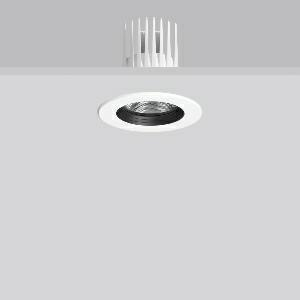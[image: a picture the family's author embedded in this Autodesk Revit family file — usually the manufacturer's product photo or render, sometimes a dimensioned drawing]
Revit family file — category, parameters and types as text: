
# Revit family: heledon_mini_e_901750_002_2_9171
name_source: partatom
category: Lighting Fixtures
units: mm (PartAtom-declared; Revit-internal decimal feet)

## family parameters
Cut with Voids When Loaded = No
Host = Face
Light Source = No
Part Type = Normal
Room Calculation Point = No
Round Connector Dimension = Use Diameter
Shared = No

## types (1)
- HELEDON mini E (1 x LED Modul 927, 3500 lm, 2700)
    Apparent Load = 29 VA
    Approval mark = CE
    CIE Flux Codes = 95 99 100 100 100
    Color Rendering = 92
    Color Temperature = 2700
    Default Elevation = 1800 mm
    Description = Series: HELEDON mini
Round recessed downlight. Housing: die-cast aluminium, powder-coated. Black plastic ring and recessed LED to prevent glare from the side. Optical assembly with reflector made of MIRO-Silver with 98% total light reflection for outstanding efficiency - can be changed without tools. Best colour rendering index Ra>90. Suitable for Recessed ceiling mounting. Installation without tools thanks to spring fastening system. Including separate LED converter with connecting cable 600 mm.High quality converter without flickering and stroboscopic effect. Through-wiring box (5 pole) available as accessory. The following accessories can be mounted without use of tools: interchangeable lenses, decorative glasses, honeycomb louvre, clear and frosted diffusers, white interchangeable plastic ring. 
Colour: traffic white, matt (RAL 9016)
Diameter: 124 mm
Height: 3 mm
Cut-out diameter: 114 mm
Recess height: 170 mm
Luminaire: recess height: 120 mm
Lamp: LED
Socket: without socket
Colour temperature: 2700K
Colour rendering index (CRI): 92
System power: 29 W
Rated luminous flux: 3500 lm
Luminous efficiency: 121 lm/W
Control gear: Regulated power supply
Protection class: II
Type of protection: IP 20
    Height = 0 mm  [stored 0 ft]
    Lamp = 1 x LED Modul 927
    Lamp Light Flux = 3500 lm
    Lamp count = 1
    Length = 124 mm  [stored 0.406824 ft]
    Lifetime = 50000 h
    Luminous efficacy = 121 lm/W
    Manufacturer = RZB
    ModVariant = No
    Model = 901750.002.2
    Mounting Place = Ceiling
    Mounting Type = Recessed
    Number of Poles = 1
    OnlyDefault = Yes
    Power Factor = 1
    Product Name = HELEDON mini E
    Product group = Recessed downlights
    ProductGroupID = 402
    Protection Class = Protection class II
    Protection Degree = IP 20
    RLX_Detail_Level = 1
    RLX_Emergency_Light_Flux = 0 lm
    RLX_Emergency_Type = 0
    RLX_Emergency_Type_DB = No
    RlxData = <blob elided: 126701 chars, md5=6fed3184>
    Socket = socket
    Standby Power = 0 W
    System Light Flux = 3500 lm
    System Power = 29 W
    Type Comments = Product without accessories
    Type Image = 901657.002.jpg
    URL = http://relux.com
    VarID = ---
    Voltage = 230 V
    Voltage Range = 220-240 V
    Weight = 0.00 kg
    Width = 0 mm  [stored 0 ft]

note: [stored X ft] marks values corroborated as IEEE doubles in the binary element streams (Revit-internal decimal feet)

## geometry (parser evidence)
native form markers: Blend x4, Sweep x10
no freeform markers — native parametric forms only
